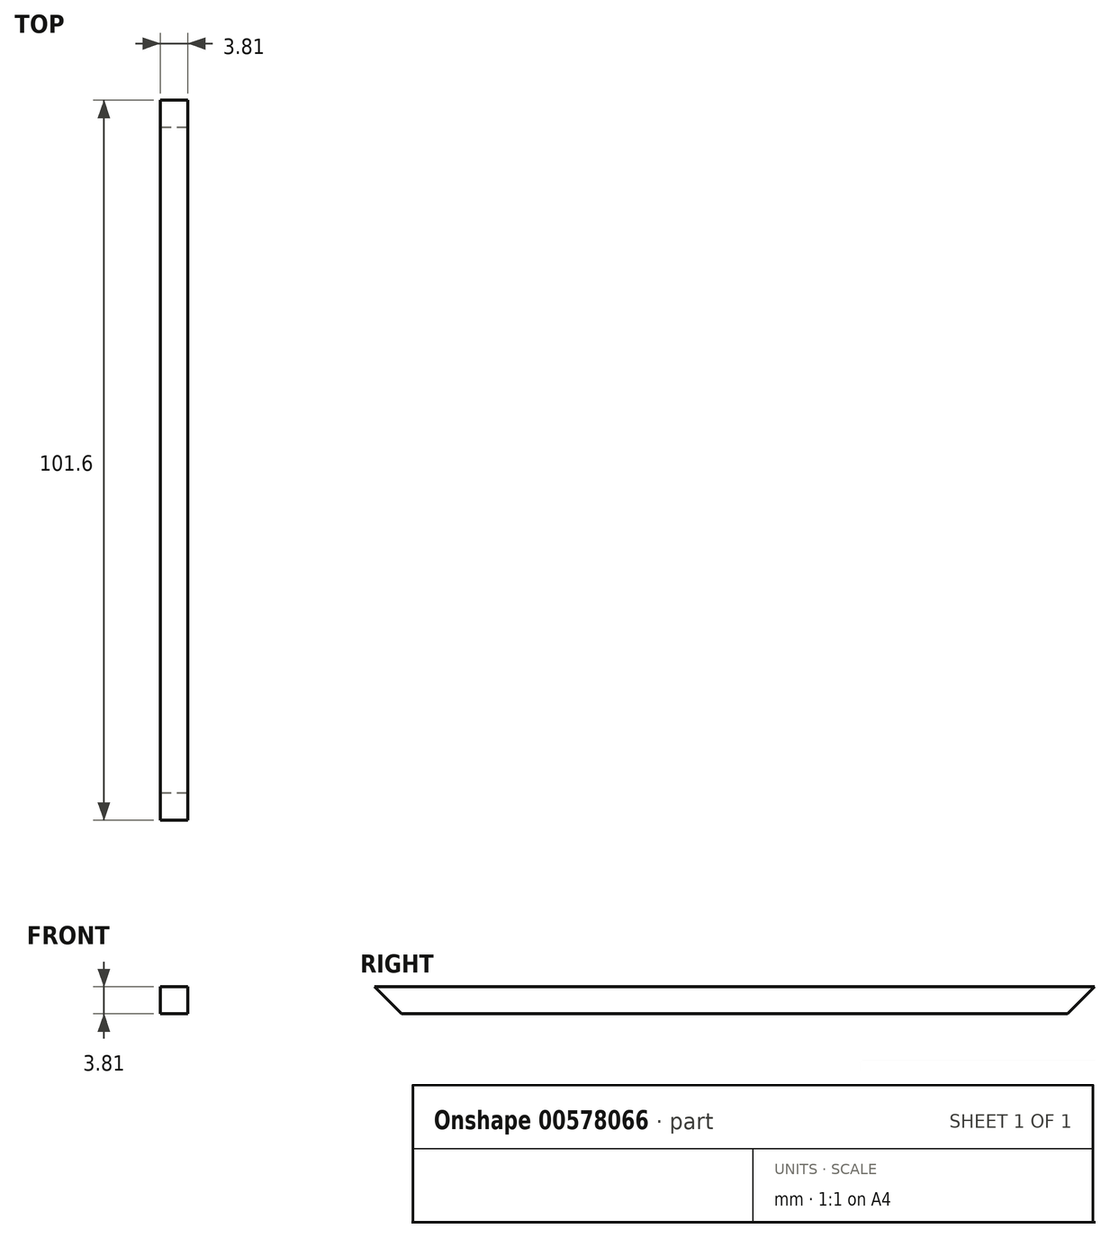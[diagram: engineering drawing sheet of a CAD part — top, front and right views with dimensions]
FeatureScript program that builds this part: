
annotation { "Feature Type Name" : "Feature", "Feature Type Description" : "" }
export const myFeature = defineFeature(function(context is Context, id is Id, definition is map)
    precondition{}
    {
        {
            var Q0;
            Q0=qCreatedBy(makeId("Top.planeOp"),FACE);
            var sketch = newSketch(context, id + "F0", { "sketchPlane" : qUnion([Q0])});
            skLineSegment(sketch, "E0.bottom", {"start": v(48.06, 96.08) * mm, "end": v(51.87, 96.08) * mm});
            skLineSegment(sketch, "E0.top", {"start": v(48.06, -5.52) * mm, "end": v(51.87, -5.52) * mm});
            skLineSegment(sketch, "E0.left", {"start": v(48.06, 96.08) * mm, "end": v(48.06, -5.52) * mm});
            skLineSegment(sketch, "E0.right", {"start": v(51.87, 96.08) * mm, "end": v(51.87, -5.52) * mm});
            skSolve(sketch);
        }
        {
            var Q0;
            Q0 = qSketchRegion(id + "F0", true);
            extrude(context, id + "F1", {"entities" : qUnion([Q0]), "depth" : 3.8 * mm, "offsetDistance" : 25.4 * mm});
        }
        {
            var Q0;
            Q0=makeQuery(id+"F1.opExtrude","CAP_EDGE",EDGE,{"disambiguationData":[OSD([sQuery(id+"F0.wireOp",EDGE,"E0.top")])],"isStart":true});
            chamfer(context, id + "F2", {"entities" : qUnion([Q0]), "width" : 3.8 * mm, "tangentPropagation" : true});
        }
        {
            var Q0;
            Q0=makeQuery(id+"F1.opExtrude","CAP_EDGE",EDGE,{"disambiguationData":[OSD([sQuery(id+"F0.wireOp",EDGE,"E0.bottom")])],"isStart":true});
            chamfer(context, id + "F3", {"entities" : qUnion([Q0]), "width" : 3.8 * mm, "tangentPropagation" : true});
        }
    });
